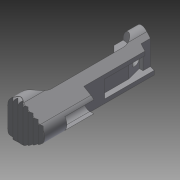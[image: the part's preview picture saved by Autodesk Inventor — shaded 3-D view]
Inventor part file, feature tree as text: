
AUTODESK INVENTOR PART (.ipt)
format: ipt  version: 2014 SP1 (Build 180222100, 222)  size: 333,824 bytes
history: native  units: in
note: dims shown in document units (in); Inventor stores cm internally (conversion verified against a paired STEP export)
features: sketch x11, extrude x10, projected_geometry x9, other x1, plane x1, fillet x1, pattern_linear x1, revolve x1
ambient origin geometry x8: Origin, YZ Plane, XZ Plane, XY Plane, X Axis, Y Axis, Z Axis, Center Point
bodies: Solid1 (feature_tree)
feature tree (35):
  extrude  "Extrusion1"  Depth=0.3385in
  other  "Work Point1"
  extrude  "Extrusion3"  Depth=0.0938in
  extrude  "Extrusion5"  Depth=0.98in
  extrude  "Extrusion6"  TaperAngle=15.0deg  [1 undecoded]
  plane  "Work Plane1"
  extrude  "Extrusion7"  Depth=0.085in
  extrude  "Extrusion8"  Depth=1.2245in TaperAngle=0.0deg
  extrude  "Extrusion9"  Depth=1.2245in TaperAngle=0.0deg
  extrude  "Extrusion10"  Depth=0.69in
  extrude  "Extrusion11"  Depth=0.07in
  fillet  "Fillet1"  Radius=0.135in
  extrude  "Extrusion12"  Depth=0.1645in TaperAngle=0.0deg
  pattern_linear  "Rectangular Pattern1"  Spacing1=0.21in  [1 undecoded]
  revolve  "Revolution1"  [1 undecoded]
  sketch  "Sketch1"  dims[d0=60.0deg d1=0.3385in]
  sketch  "Sketch3"  dims[d2=0.1515in d3=0.0938in]
  sketch  "Sketch5"  dims[d4=1.2245in d5=0.0in d10=0.98in]
  sketch  "Sketch6"  dims[d12=1.2245in d13=0.0in d18=15.0deg]
  sketch  "Sketch7"  dims[d19=1.2245in d20=0.0in d21=0.085in]
  projected_geometry  "Projected Loop1"
  sketch  "Sketch8"  dims[d22=0.4925in d23=1.2245in d24=0.0in]
  sketch  "Sketch9"  dims[d25=-0.217in d26=1.2245in d27=0.0in]
  projected_geometry  "Projected Loop2"
  sketch  "Sketch10"  dims[d28=0.05in d29=0.69in]
  sketch  "Sketch11"  dims[d30=15.0deg d32=0.07in d33=0.135in]
  sketch  "Sketch13"  dims[d34=0.1645in d35=0.0in d36=0.1645in d37=0.0in]
  sketch  "Sketch14"  dims[d38=45.0deg d39=0.21in d40=0.155in d41=0.0in d42=0.155in d43=0.0in d44=0.0075in d45=0.3359in d46=90.0deg d47=0.048in d48=1.0in d49=0.0in d50=2.7559in d52=0.048in d53=0.0298in d54=90.0deg]
  projected_geometry  "Project Cut Edges2"
  projected_geometry  "Project Cut Edges4"
  projected_geometry  "Project Cut Edges5"
  projected_geometry  "Project Cut Edges6"
  projected_geometry  "Project Cut Edges7"
  projected_geometry  "Project Cut Edges9"
  projected_geometry  "Project Cut Edges10"
note: 3 required parameter values undecoded (feature->parameter linkage not recoverable at this tier; creation-order binding heuristic only, values carry confidence <= 0.55)